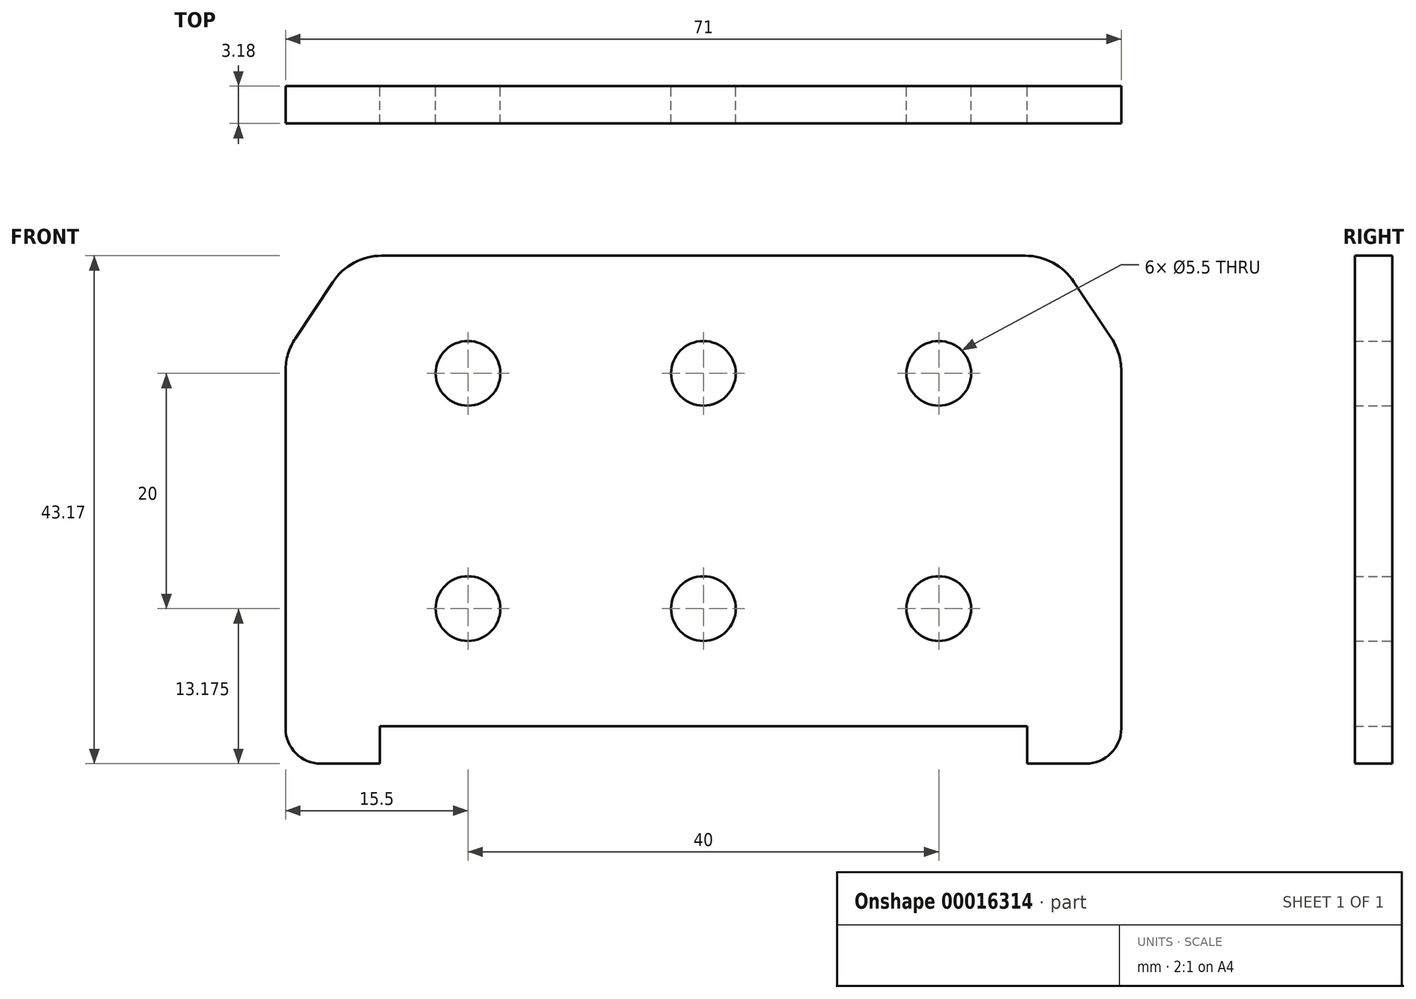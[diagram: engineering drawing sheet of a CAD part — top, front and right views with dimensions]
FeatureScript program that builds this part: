
annotation { "Feature Type Name" : "Feature", "Feature Type Description" : "" }
export const myFeature = defineFeature(function(context is Context, id is Id, definition is map)
    precondition{}
    {
        {
            var Q0;
            Q0=qCreatedBy(makeId("Front.planeOp"),FACE);
            var sketch = newSketch(context, id + "F0", { "sketchPlane" : qUnion([Q0])});
            skLineSegment(sketch, "E0.bottom", {"start": v(-30, 0) * mm, "end": v(30, 0) * mm, "construction": true});
            skLineSegment(sketch, "E0.top", {"start": v(-30, 48.1) * mm, "end": v(30, 48.1) * mm, "construction": true});
            skLineSegment(sketch, "E0.left", {"start": v(-30, 0) * mm, "end": v(-30, 48.1) * mm, "construction": true});
            skLineSegment(sketch, "E0.right", {"start": v(30, 0) * mm, "end": v(30, 48.1) * mm, "construction": true});
            skLineSegment(sketch, "E1", {"start": v(0, 0) * mm, "end": v(0, -10) * mm, "construction": true});
            skLineSegment(sketch, "E2", {"start": v(-27.32, 43.18) * mm, "end": v(27.32, 43.18) * mm});
            skCircle(sketch, "E3", {"center": v(-20, 33.18) * mm, "radius": 2.75 * mm});
            skCircle(sketch, "E4", {"center": v(-20, 13.18) * mm, "radius": 2.75 * mm});
            skCircle(sketch, "E5", {"center": v(0, 33.18) * mm, "radius": 2.75 * mm});
            skCircle(sketch, "E6", {"center": v(0, 13.18) * mm, "radius": 2.75 * mm});
            skLineSegment(sketch, "E7", {"start": v(0, 33.18) * mm, "end": v(-20, 33.18) * mm, "construction": true});
            skCircle(sketch, "E8.MirrorC", {"center": v(20, 13.18) * mm, "radius": 2.75 * mm});
            skCircle(sketch, "E9.MirrorC", {"center": v(20, 33.18) * mm, "radius": 2.75 * mm});
            skLineSegment(sketch, "E10", {"start": v(-20, 33.18) * mm, "end": v(-20, 13.18) * mm, "construction": true});
            skLineSegment(sketch, "E11", {"start": v(-20, 33.18) * mm, "end": v(-20, 43.18) * mm, "construction": true});
            skLineSegment(sketch, "E12", {"start": v(-20, 0) * mm, "end": v(-20, -10) * mm, "construction": true});
            skLineSegment(sketch, "E13", {"start": v(-30, 0) * mm, "end": v(-45, 0) * mm, "construction": true});
            skLineSegment(sketch, "E14.top", {"start": v(-27.5, 3.18) * mm, "end": v(27.5, 3.17) * mm});
            skLineSegment(sketch, "E14.left", {"start": v(-27.5, 0) * mm, "end": v(-27.5, 3.17) * mm});
            skLineSegment(sketch, "E14.right", {"start": v(27.5, 0) * mm, "end": v(27.5, 3.18) * mm});
            skPoint(sketch, "E15", {"position": v(0, -3.18) * mm});
            skPoint(sketch, "E16", {"position": v(27.5, 0) * mm});
            skLineSegment(sketch, "E17", {"start": v(-20, 13.18) * mm, "end": v(-20, 3.18) * mm, "construction": true});
            skPoint(sketch, "E18.visualSharp", {"position": v(-30, 43.18) * mm});
            skPoint(sketch, "E19.visualSharp", {"position": v(30, 43.18) * mm});
            skLineSegment(sketch, "E20", {"start": v(-27.5, 0) * mm, "end": v(-32.5, 0) * mm});
            skLineSegment(sketch, "E21", {"start": v(-35.5, 3) * mm, "end": v(-35.5, 33.38) * mm});
            skLineSegment(sketch, "E22", {"start": v(27.5, 0) * mm, "end": v(32.5, 0) * mm});
            skLineSegment(sketch, "E23", {"start": v(35.5, 3) * mm, "end": v(35.5, 33.38) * mm});
            skPoint(sketch, "E24.orphan", {"position": v(27.5, -3.18) * mm});
            skPoint(sketch, "E25.orphan", {"position": v(-27.5, -3.18) * mm});
            skPoint(sketch, "E26.visualSharp", {"position": v(35.5, 0) * mm});
            skArc(sketch, "E26.filletArc", {"start": v(32.5, 0) * mm, "mid": v(34.62, 0.88) * mm, "end": v(35.5, 3) * mm});
            skPoint(sketch, "E27.visualSharp", {"position": v(-35.5, 0) * mm});
            skArc(sketch, "E27.filletArc", {"start": v(-35.5, 3) * mm, "mid": v(-34.62, 0.88) * mm, "end": v(-32.5, 0) * mm});
            skLineSegment(sketch, "E28.MirrorCS", {"start": v(34.67, 36.15) * mm, "end": v(31.48, 40.94) * mm});
            skLineSegment(sketch, "E29.MirrorCS", {"start": v(81.43, 54.07) * mm, "end": v(90.65, 50.2) * mm});
            skLineSegment(sketch, "E30.MirrorCS", {"start": v(-34.67, 36.15) * mm, "end": v(-31.48, 40.94) * mm});
            skArc(sketch, "E31.filletArc", {"start": v(-27.32, 43.18) * mm, "mid": v(-29.68, 42.58) * mm, "end": v(-31.48, 40.94) * mm});
            skArc(sketch, "E32.filletArc", {"start": v(31.48, 40.94) * mm, "mid": v(29.68, 42.58) * mm, "end": v(27.32, 43.18) * mm});
            skPoint(sketch, "E33.visualSharp", {"position": v(35.5, 34.9) * mm});
            skArc(sketch, "E33.filletArc", {"start": v(35.5, 33.38) * mm, "mid": v(35.29, 34.83) * mm, "end": v(34.67, 36.15) * mm});
            skPoint(sketch, "E34.visualSharp", {"position": v(-35.5, 34.9) * mm});
            skArc(sketch, "E34.filletArc", {"start": v(-34.67, 36.15) * mm, "mid": v(-35.29, 34.83) * mm, "end": v(-35.5, 33.38) * mm});
            skSolve(sketch);
        }
        {
            var Q0;
            Q0=qSketchRegion(id+"F0",true);
            extrude(context, id + "F1", {"entities" : qUnion([Q0]), "endBound" : BoundingType.SYMMETRIC, "depth" : 3.17 * mm});
        }
    });
